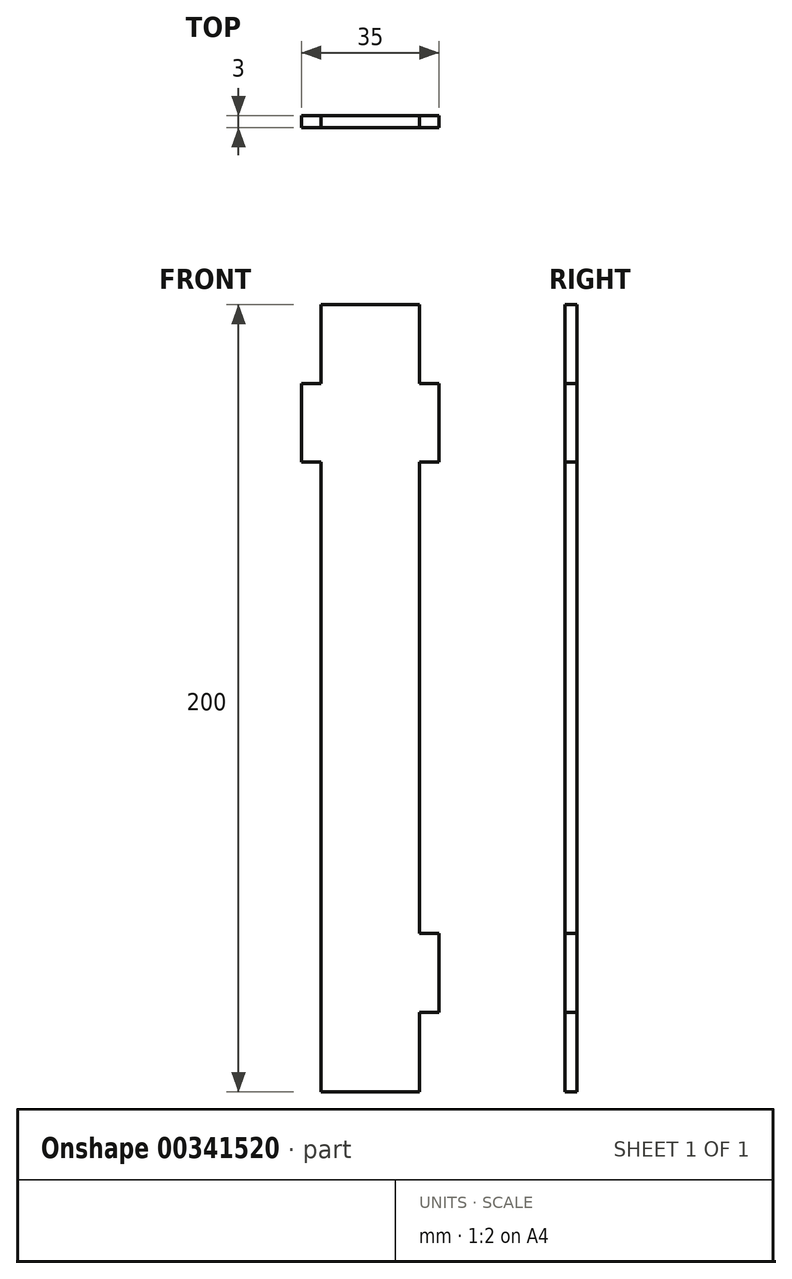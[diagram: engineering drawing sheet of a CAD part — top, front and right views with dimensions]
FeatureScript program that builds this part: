
annotation { "Feature Type Name" : "Feature", "Feature Type Description" : "" }
export const myFeature = defineFeature(function(context is Context, id is Id, definition is map)
    precondition{}
    {
        {
            var Q0;
            Q0=qCreatedBy(makeId("Front.planeOp"),FACE);
            var sketch = newSketch(context, id + "F0", { "sketchPlane" : qUnion([Q0])});
            skLineSegment(sketch, "E0", {"start": v(-25, 107.72) * mm, "end": v(-25, -92.28) * mm});
            skLineSegment(sketch, "E1", {"start": v(-25, 107.72) * mm, "end": v(0, 107.72) * mm});
            skLineSegment(sketch, "E2", {"start": v(0, 107.72) * mm, "end": v(0, -92.28) * mm});
            skLineSegment(sketch, "E3", {"start": v(0, -92.28) * mm, "end": v(-25, -92.28) * mm});
            skLineSegment(sketch, "E4", {"start": v(0, -92.28) * mm, "end": v(0, -72.28) * mm});
            skLineSegment(sketch, "E5", {"start": v(0, -72.28) * mm, "end": v(3, -72.28) * mm});
            skLineSegment(sketch, "E6", {"start": v(3, -52.04) * mm, "end": v(0, -52.04) * mm});
            skLineSegment(sketch, "E7", {"start": v(-25, -72.28) * mm, "end": v(-25, -52.28) * mm});
            skLineSegment(sketch, "E8", {"start": v(-25, -72.28) * mm, "end": v(-28, -72.28) * mm});
            skLineSegment(sketch, "E9", {"start": v(-25, -52.28) * mm, "end": v(-28, -52.28) * mm});
            skLineSegment(sketch, "E10.bottom", {"start": v(-25, -52.28) * mm, "end": v(-30, -52.28) * mm});
            skLineSegment(sketch, "E10.top", {"start": v(-25, -72.28) * mm, "end": v(-30, -72.28) * mm});
            skLineSegment(sketch, "E10.left", {"start": v(-25, -52.28) * mm, "end": v(-25, -72.28) * mm});
            skLineSegment(sketch, "E10.right", {"start": v(-30, -52.28) * mm, "end": v(-30, -72.28) * mm});
            skLineSegment(sketch, "E11.bottom", {"start": v(0, -52.04) * mm, "end": v(5, -52.04) * mm});
            skLineSegment(sketch, "E11.top", {"start": v(0, -72.04) * mm, "end": v(5, -72.04) * mm});
            skLineSegment(sketch, "E11.left", {"start": v(0, -52.04) * mm, "end": v(0, -72.04) * mm});
            skLineSegment(sketch, "E11.right", {"start": v(5, -52.04) * mm, "end": v(5, -72.04) * mm});
            skLineSegment(sketch, "E12.top", {"start": v(-25, 67.72) * mm, "end": v(-30, 67.72) * mm});
            skLineSegment(sketch, "E12.left", {"start": v(-25, 107.72) * mm, "end": v(-25, 67.72) * mm});
            skLineSegment(sketch, "E13.top", {"start": v(-25, 87.72) * mm, "end": v(-30, 87.72) * mm});
            skLineSegment(sketch, "E13.left", {"start": v(-25, 67.72) * mm, "end": v(-25, 87.72) * mm});
            skLineSegment(sketch, "E13.right", {"start": v(-30, 67.72) * mm, "end": v(-30, 87.72) * mm});
            skLineSegment(sketch, "E14.bottom", {"start": v(0, 87.72) * mm, "end": v(5, 87.72) * mm});
            skLineSegment(sketch, "E14.top", {"start": v(0, 67.72) * mm, "end": v(5, 67.72) * mm});
            skLineSegment(sketch, "E14.left", {"start": v(0, 87.72) * mm, "end": v(0, 67.72) * mm});
            skLineSegment(sketch, "E14.right", {"start": v(5, 87.72) * mm, "end": v(5, 67.72) * mm});
            skSolve(sketch);
        }
        {
            var Q0;
            {var subQ8=sQuery(id+"F0.wireOp",EDGE,"E1");Q0=makeQuery(id+"F0.imprint","IMPRINT",FACE,{"disambiguationData":[TD([[makeQuery(id+"F0.imprint","IMPRINT",EDGE,{"derivedFrom":subQ8}),-1.0]])]});}
            var Q1;
            Q1=makeQuery(id+"F0.imprint","IMPRINT",FACE,{"disambiguationData":[TD([[makeQuery(id+"F0.imprint","IMPRINT",EDGE,{"derivedFrom":sQuery(id+"F0.wireOp",EDGE,"E14.bottom")}),-1.0]])]});
            var Q2;
            Q2=makeQuery(id+"F0.imprint","IMPRINT",FACE,{"disambiguationData":[TD([[makeQuery(id+"F0.imprint","IMPRINT",EDGE,{"derivedFrom":sQuery(id+"F0.wireOp",EDGE,"E12.top")}),-1.0]])]});
            var Q3;
            Q3=makeQuery(id+"F0.imprint","IMPRINT",FACE,{"disambiguationData":[TD([[makeQuery(id+"F0.imprint","IMPRINT",EDGE,{"derivedFrom":sQuery(id+"F0.wireOp",EDGE,"E11.top")}),1.0]])]});
            var Q4;
            {var subQ0=sQuery(id+"F0.wireOp",EDGE,"E10.left");Q4=makeQuery(id+"F0.imprint","IMPRINT",FACE,{"disambiguationData":[TD([[makeQuery(id+"F0.imprint","IMPRINT",EDGE,{"derivedFrom":subQ0}),-1.0]])]});}
            extrude(context, id + "F1", {"entities" : qUnion([Q0, Q1, Q2, Q3, Q4]), "oppositeDirection" : true, "depth" : 3 * mm});
        }
    });
